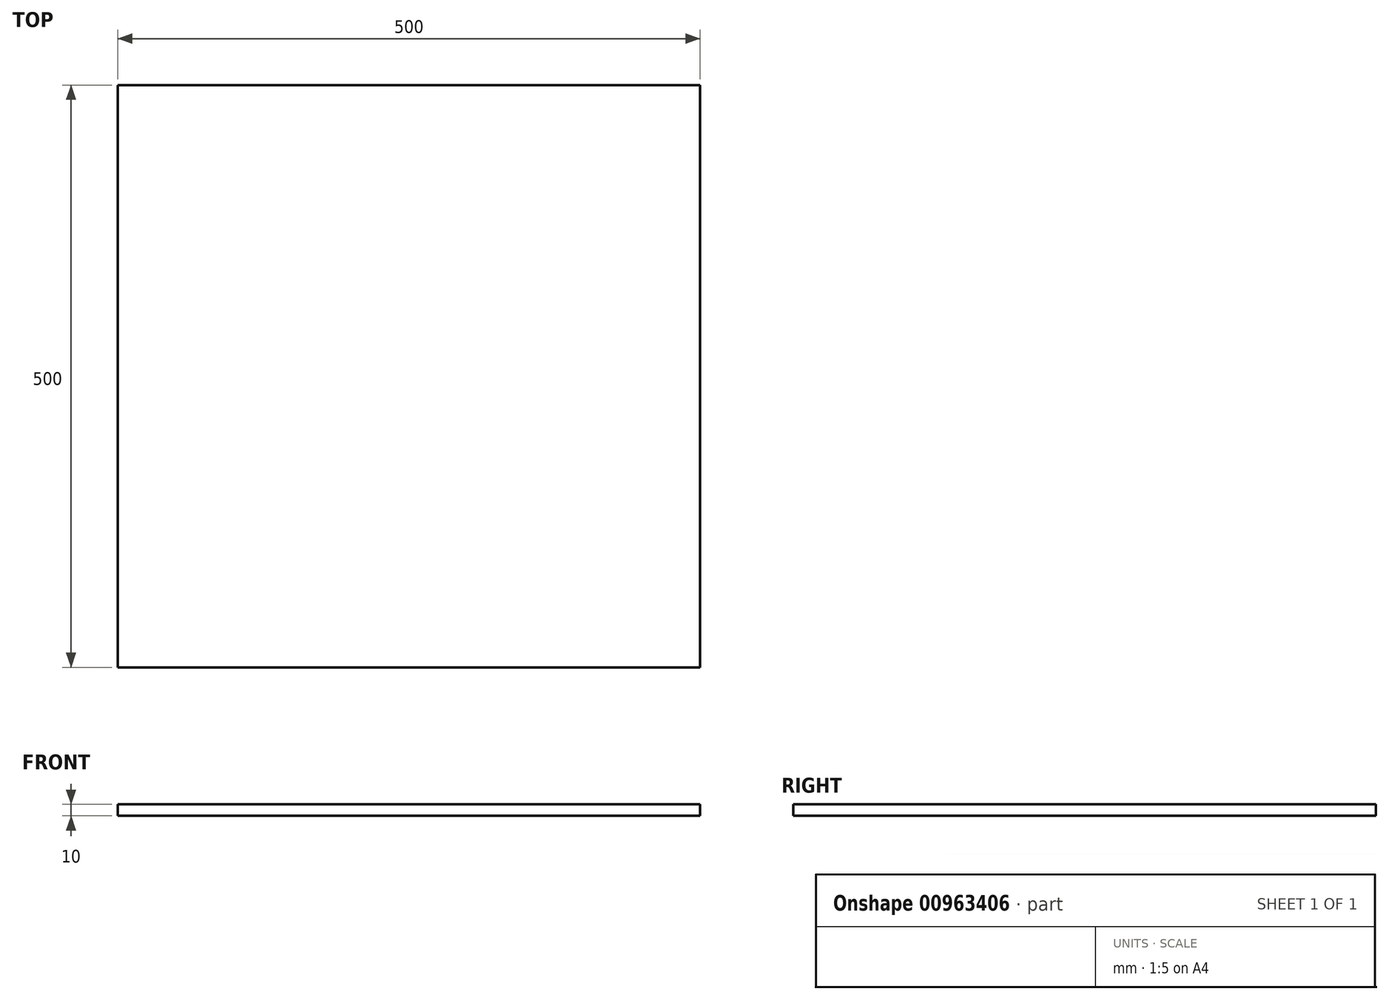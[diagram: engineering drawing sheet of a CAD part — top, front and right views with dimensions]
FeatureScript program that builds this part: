
annotation { "Feature Type Name" : "Feature", "Feature Type Description" : "" }
export const myFeature = defineFeature(function(context is Context, id is Id, definition is map)
    precondition{}
    {
        {
            var Q0;
            Q0=qCreatedBy(makeId("Top.planeOp"),FACE);
            var sketch = newSketch(context, id + "F0", { "sketchPlane" : qUnion([Q0])});
            skLineSegment(sketch, "E0.bottom", {"start": v(250, -250) * mm, "end": v(-250, -250) * mm});
            skLineSegment(sketch, "E0.top", {"start": v(250, 250) * mm, "end": v(-250, 250) * mm});
            skLineSegment(sketch, "E0.left", {"start": v(250, -250) * mm, "end": v(250, 250) * mm});
            skLineSegment(sketch, "E0.right", {"start": v(-250, -250) * mm, "end": v(-250, 250) * mm});
            skPoint(sketch, "E0.middle", {"position": v(0, 0) * mm});
            skSolve(sketch);
        }
        {
            var Q0;
            Q0 = qSketchRegion(id + "F0", true);
            extrude(context, id + "F1", {"entities" : qUnion([Q0]), "depth" : 10 * mm, "offsetDistance" : 25 * mm});
        }
    });
